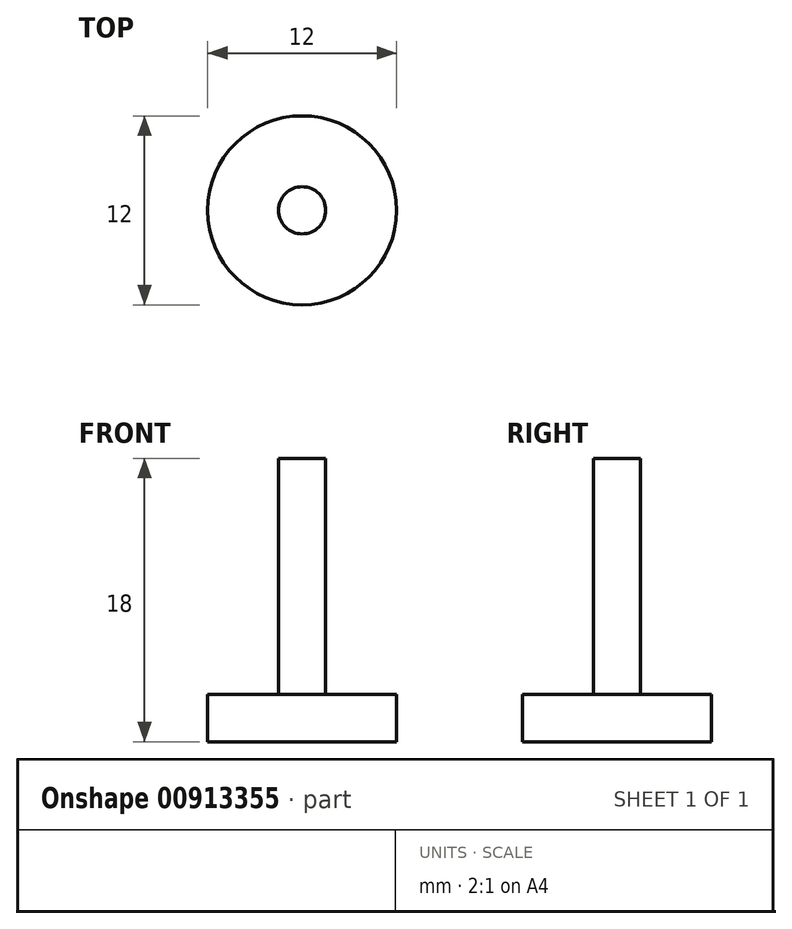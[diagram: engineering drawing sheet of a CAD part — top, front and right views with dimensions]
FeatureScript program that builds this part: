
annotation { "Feature Type Name" : "Feature", "Feature Type Description" : "" }
export const myFeature = defineFeature(function(context is Context, id is Id, definition is map)
    precondition{}
    {
        {
            var Q0;
            Q0=qCreatedBy(makeId("Front.planeOp"),FACE);
            var sketch = newSketch(context, id + "F0", { "sketchPlane" : qUnion([Q0])});
            skLineSegment(sketch, "E0", {"start": v(0, 0) * mm, "end": v(6, 0) * mm});
            skLineSegment(sketch, "E1", {"start": v(6, 0) * mm, "end": v(6, 3) * mm});
            skLineSegment(sketch, "E2", {"start": v(6, 3) * mm, "end": v(1.5, 3) * mm});
            skLineSegment(sketch, "E3", {"start": v(1.5, 3) * mm, "end": v(1.5, 18) * mm});
            skLineSegment(sketch, "E4", {"start": v(1.5, 18) * mm, "end": v(0, 18) * mm});
            skLineSegment(sketch, "E5", {"start": v(0, 18) * mm, "end": v(0, 0) * mm});
            skSolve(sketch);
        }
        {
            var Q0;
            Q0 = qSketchRegion(id + "F0", true);
            var Q1;
            Q1=sQuery(id+"F0.wireOp",EDGE,"E5");
            revolve(context, id + "F1", {"surfaceOperationType" : NewSurfaceOperationType.NEW, "entities" : qUnion([Q0]), "axis" : qUnion([Q1]), "revolveType" : RevolveType.FULL});
        }
    });
